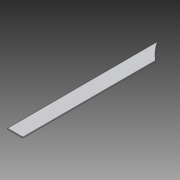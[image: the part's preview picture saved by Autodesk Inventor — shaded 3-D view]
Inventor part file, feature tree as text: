
AUTODESK INVENTOR PART (.ipt)
format: ipt  version: 2014 SP1 (Build 180222100, 222)  size: 75,264 bytes
history: native  units: in
note: dims shown in document units (in); Inventor stores cm internally (conversion verified against a paired STEP export)
features: extrude x1, sketch x1
ambient origin geometry x8: Origin, YZ Plane, XZ Plane, XY Plane, X Axis, Y Axis, Z Axis, Center Point
bodies: Solid1 (feature_tree)
feature tree (2):
  extrude  "Extrusion1"  Depth=0.0625in
  sketch  "Sketch1"  dims[d0=11.5in d1=13.0in d2=13.0in d6=1.0in d10=9.5in d11=0.0625in d12=0.0in]
